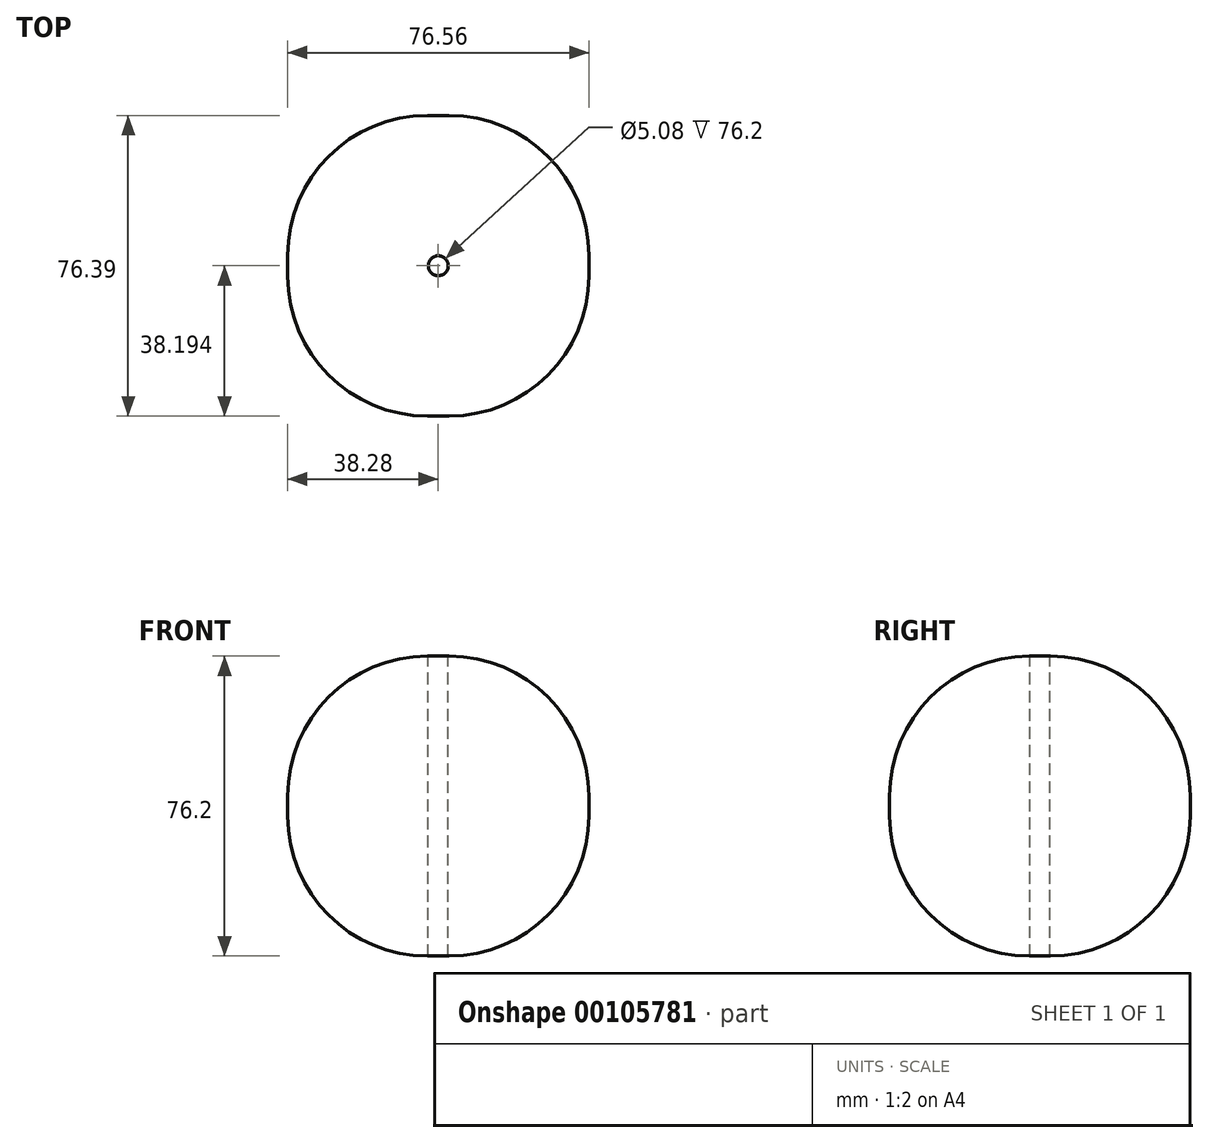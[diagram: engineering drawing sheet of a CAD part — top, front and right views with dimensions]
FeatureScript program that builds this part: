
annotation { "Feature Type Name" : "Feature", "Feature Type Description" : "" }
export const myFeature = defineFeature(function(context is Context, id is Id, definition is map)
    precondition{}
    {
        {
            var Q0;
            Q0=qCreatedBy(makeId("Top.planeOp"),FACE);
            var sketch = newSketch(context, id + "F1", { "sketchPlane" : qUnion([Q0])});
            skLineSegment(sketch, "E0.bottom", {"start": v(0, 0) * mm, "end": v(76.56, 0) * mm});
            skLineSegment(sketch, "E0.top", {"start": v(0, 76.39) * mm, "end": v(76.56, 76.39) * mm});
            skLineSegment(sketch, "E0.left", {"start": v(0, 0) * mm, "end": v(0, 76.39) * mm});
            skLineSegment(sketch, "E0.right", {"start": v(76.56, 0) * mm, "end": v(76.56, 76.39) * mm});
            skSolve(sketch);
        }
        {
            var Q0;
            Q0 = qSketchRegion(id + "F1", true);
            var Q1;
            Q1=makeQuery(id+"F1.imprint","IMPRINT",FACE,{"disambiguationData":[TD([[makeQuery(id+"F1.imprint","IMPRINT",EDGE,{"derivedFrom":sQuery(id+"F1.wireOp",EDGE,"E0.bottom")}),1.0]])]});
            extrude(context, id + "F2", {"entities" : qUnion([Q0, Q1]), "depth" : 76.2 * mm});
        }
        {
            var Q0;
            Q0=makeQuery(id+"F2.opExtrude","SWEPT_FACE",FACE,{"disambiguationData":[OSD([sQuery(id+"F1.wireOp",EDGE,"E0.top")])]});
            var Q1;
            Q1=makeQuery(id+"F2.opExtrude","CAP_EDGE",EDGE,{"disambiguationData":[OSD([sQuery(id+"F1.wireOp",EDGE,"E0.bottom")])],"isStart":false});
            var Q2;
            Q2=makeQuery(id+"F2.opExtrude","CAP_EDGE",EDGE,{"disambiguationData":[OSD([sQuery(id+"F1.wireOp",EDGE,"E0.left")])],"isStart":false});
            var Q3;
            Q3=makeQuery(id+"F2.opExtrude","SWEPT_EDGE",EDGE,{"disambiguationData":[OSD([sQuery(id+"F1.wireOp",EDGE,"E0.bottom"),sQuery(id+"F1.wireOp",EDGE,"E0.right")])]});
            var Q4;
            Q4=makeQuery(id+"F2.opExtrude","CAP_EDGE",EDGE,{"disambiguationData":[OSD([sQuery(id+"F1.wireOp",EDGE,"E0.left")])],"isStart":true});
            var Q5;
            Q5=makeQuery(id+"F2.opExtrude","SWEPT_EDGE",EDGE,{"disambiguationData":[OSD([sQuery(id+"F1.wireOp",EDGE,"E0.bottom"),sQuery(id+"F1.wireOp",EDGE,"E0.left")])]});
            var Q6;
            Q6=makeQuery(id+"F2.opExtrude","CAP_FACE",FACE,{"disambiguationData":[OSD([sQuery(id+"F1.wireOp",EDGE,"E0.bottom"),sQuery(id+"F1.wireOp",EDGE,"E0.top"),sQuery(id+"F1.wireOp",EDGE,"E0.left"),sQuery(id+"F1.wireOp",EDGE,"E0.right")])],"isStart":true});
            var Q7;
            Q7=makeQuery(id+"F2.opExtrude","CAP_EDGE",EDGE,{"disambiguationData":[OSD([sQuery(id+"F1.wireOp",EDGE,"E0.bottom")])],"isStart":true});
            var Q8;
            Q8=makeQuery(id+"F2.opExtrude","CAP_EDGE",EDGE,{"disambiguationData":[OSD([sQuery(id+"F1.wireOp",EDGE,"E0.right")])],"isStart":false});
            fillet(context, id + "F3", {"entities" : qUnion([Q0, Q1, Q2, Q3, Q4, Q5, Q6, Q7, Q8]), "radius" : 35.56 * mm, "tangentPropagation" : true, "allowEdgeOverflow" : false});
        }
        {
            var Q0;
            Q0=makeQuery(id+"F2.opExtrude","CAP_FACE",FACE,{"disambiguationData":[OSD([sQuery(id+"F1.wireOp",EDGE,"E0.bottom"),sQuery(id+"F1.wireOp",EDGE,"E0.top"),sQuery(id+"F1.wireOp",EDGE,"E0.left"),sQuery(id+"F1.wireOp",EDGE,"E0.right")])],"isStart":false});
            var sketch = newSketch(context, id + "F4", { "sketchPlane" : qUnion([Q0])});
            skLineSegment(sketch, "E1", {"start": v(35.56, 40.83) * mm, "end": v(38.28, 40.83) * mm});
            skLineSegment(sketch, "E2", {"start": v(38.28, 40.83) * mm, "end": v(38.28, 40.83) * mm});
            skLineSegment(sketch, "E3", {"start": v(35.56, 38.2) * mm, "end": v(35.56, 40.83) * mm});
            skLineSegment(sketch, "E4", {"start": v(38.28, 35.56) * mm, "end": v(38.28, 40.83) * mm});
            skLineSegment(sketch, "E5", {"start": v(38.28, 38.2) * mm, "end": v(35.56, 38.2) * mm});
            skSolve(sketch);
        }
        {
            var Q0;
            Q0=sQuery(id+"F4.wireOp",VERTEX,"E5.start");
            var Q1;
            Q1=makeQuery(id+"F2.opExtrude","SWEPT_BODY",BODY,{"disambiguationData":[OSD([sQuery(id+"F1.wireOp",EDGE,"E0.bottom"),sQuery(id+"F1.wireOp",EDGE,"E0.top"),sQuery(id+"F1.wireOp",EDGE,"E0.left"),sQuery(id+"F1.wireOp",EDGE,"E0.right")])]});
            hole(context, id + "F0", {"style" : HoleStyle.SIMPLE, "endStyle" : HoleEndStyle.THROUGH, "holeDiameter" : 5.08 * mm, "locations" : qUnion([Q0]), "scope" : qUnion([Q1]), "isTappedThrough" : true});
        }
    });
